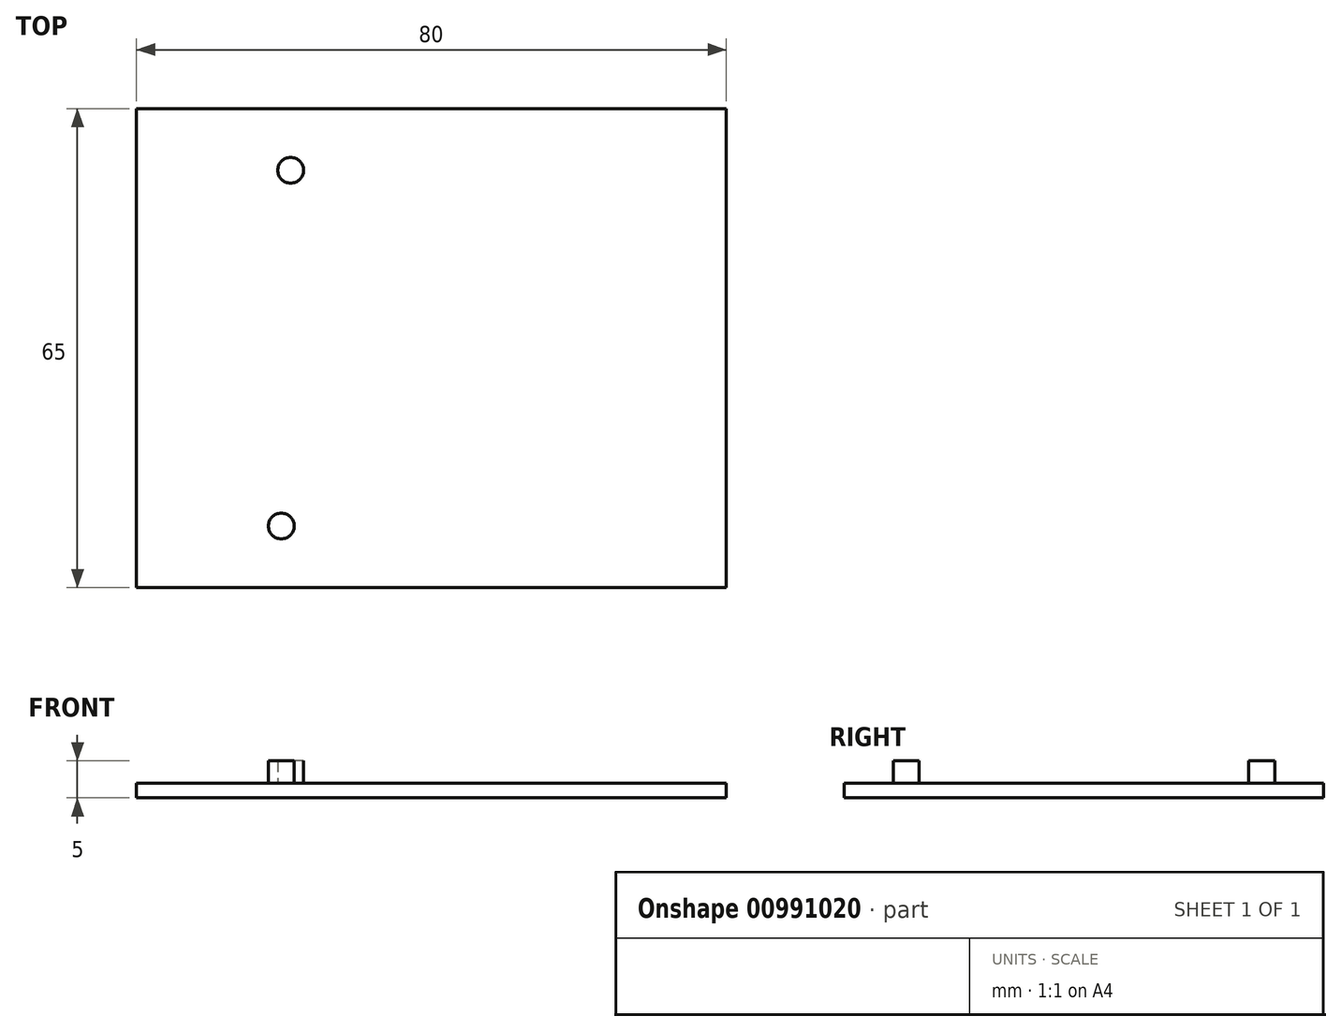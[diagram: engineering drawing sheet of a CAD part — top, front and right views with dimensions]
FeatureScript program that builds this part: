
annotation { "Feature Type Name" : "Feature", "Feature Type Description" : "" }
export const myFeature = defineFeature(function(context is Context, id is Id, definition is map)
    precondition{}
    {
        {
            var Q0;
            Q0=qCreatedBy(makeId("Top.planeOp"),FACE);
            var sketch = newSketch(context, id + "F0", { "sketchPlane" : qUnion([Q0])});
            skLineSegment(sketch, "E0.bottom", {"start": v(40, -32.5) * mm, "end": v(-40, -32.5) * mm});
            skLineSegment(sketch, "E0.top", {"start": v(40, 32.5) * mm, "end": v(-40, 32.5) * mm});
            skLineSegment(sketch, "E0.left", {"start": v(40, -32.5) * mm, "end": v(40, 32.5) * mm});
            skLineSegment(sketch, "E0.right", {"start": v(-40, -32.5) * mm, "end": v(-40, 32.5) * mm});
            skPoint(sketch, "E0.middle", {"position": v(0, 0) * mm});
            skSolve(sketch);
        }
        {
            var Q0;
            Q0=makeQuery(id+"F0.imprint","IMPRINT",FACE,{"disambiguationData":[TD([[makeQuery(id+"F0.imprint","IMPRINT",EDGE,{"derivedFrom":sQuery(id+"F0.wireOp",EDGE,"E0.bottom")}),-1.0]])]});
            extrude(context, id + "F1", {"entities" : qUnion([Q0]), "depth" : 2 * mm, "offsetDistance" : 25 * mm});
        }
        {
            var Q0;
            Q0=makeQuery(id+"F1.opExtrude","CAP_FACE",FACE,{"disambiguationData":[OSD([sQuery(id+"F0.wireOp",EDGE,"E0.bottom"),sQuery(id+"F0.wireOp",EDGE,"E0.top"),sQuery(id+"F0.wireOp",EDGE,"E0.left"),sQuery(id+"F0.wireOp",EDGE,"E0.right")])],"isStart":false});
            var sketch = newSketch(context, id + "F2", { "sketchPlane" : qUnion([Q0])});
            skLineSegment(sketch, "E1", {"start": v(-19.1, 24.13) * mm, "end": v(-19.1, -24.13) * mm, "construction": true});
            skCircle(sketch, "E2", {"center": v(-19.1, 24.13) * mm, "radius": 1.75 * mm});
            skPoint(sketch, "E3", {"position": v(-19.1, 0) * mm});
            skLineSegment(sketch, "E4", {"start": v(-40, 0) * mm, "end": v(40, 0) * mm});
            skLineSegment(sketch, "E5", {"start": v(-20.37, -24.13) * mm, "end": v(-19.1, -24.13) * mm, "construction": true});
            skCircle(sketch, "E6", {"center": v(-20.37, -24.13) * mm, "radius": 1.75 * mm});
            skSolve(sketch);
        }
        {
            var Q0;
            Q0 = qSketchRegion(id + "F2", true);
            extrude(context, id + "F3", {"entities" : qUnion([Q0]), "operationType" : NewBodyOperationType.ADD, "depth" : 3 * mm, "offsetDistance" : 25 * mm});
        }
    });
